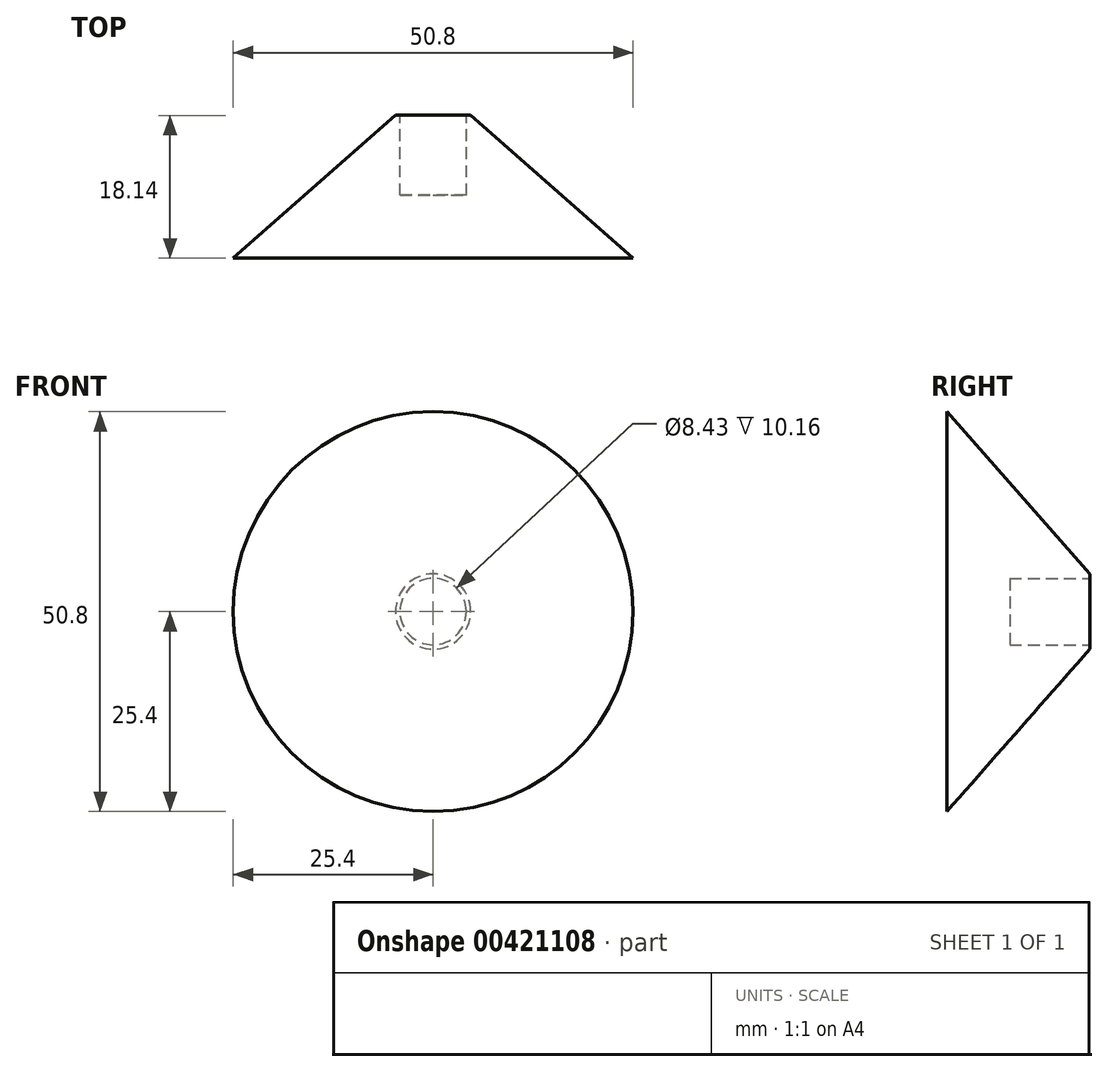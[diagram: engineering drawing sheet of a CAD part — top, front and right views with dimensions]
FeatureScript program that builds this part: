
annotation { "Feature Type Name" : "Feature", "Feature Type Description" : "" }
export const myFeature = defineFeature(function(context is Context, id is Id, definition is map)
    precondition{}
    {
        {
            var Q0;
            Q0=qCreatedBy(makeId("Top.planeOp"),FACE);
            var sketch = newSketch(context, id + "F0", { "sketchPlane" : qUnion([Q0])});
            skLineSegment(sketch, "E0", {"start": v(0, 0) * mm, "end": v(25.4, 0) * mm});
            skLineSegment(sketch, "E1", {"start": v(0, 0) * mm, "end": v(0, 18.14) * mm});
            skLineSegment(sketch, "E2", {"start": v(0, 18.14) * mm, "end": v(4.77, 18.14) * mm});
            skLineSegment(sketch, "E3", {"start": v(25.4, 0) * mm, "end": v(4.77, 18.14) * mm});
            skSolve(sketch);
        }
        {
            var Q0;
            Q0=makeQuery(id+"F0.imprint","IMPRINT",FACE,{"disambiguationData":[TD([[makeQuery(id+"F0.imprint","IMPRINT",EDGE,{"derivedFrom":sQuery(id+"F0.wireOp",EDGE,"E0")}),1.0]])]});
            var Q1;
            Q1=sQuery(id+"F0.wireOp",EDGE,"E1");
            revolve(context, id + "F1", {"entities" : qUnion([Q0]), "axis" : qUnion([Q1]), "revolveType" : RevolveType.FULL});
        }
        {
            var Q0;
            Q0=makeQuery(id+"F1.opRevolve","SWEPT_FACE",FACE,{"disambiguationData":[OSD([sQuery(id+"F0.wireOp",EDGE,"E2")])]});
            var sketch = newSketch(context, id + "F2", { "sketchPlane" : qUnion([Q0])});
            skCircle(sketch, "E4", {"center": v(0, 0) * mm, "radius": 4.22 * mm});
            skSolve(sketch);
        }
        {
            var Q0;
            Q0 = qSketchRegion(id + "F2", true);
            extrude(context, id + "F3", {"entities" : qUnion([Q0]), "operationType" : NewBodyOperationType.REMOVE, "oppositeDirection" : true, "depth" : 10.16 * mm});
        }
    });
